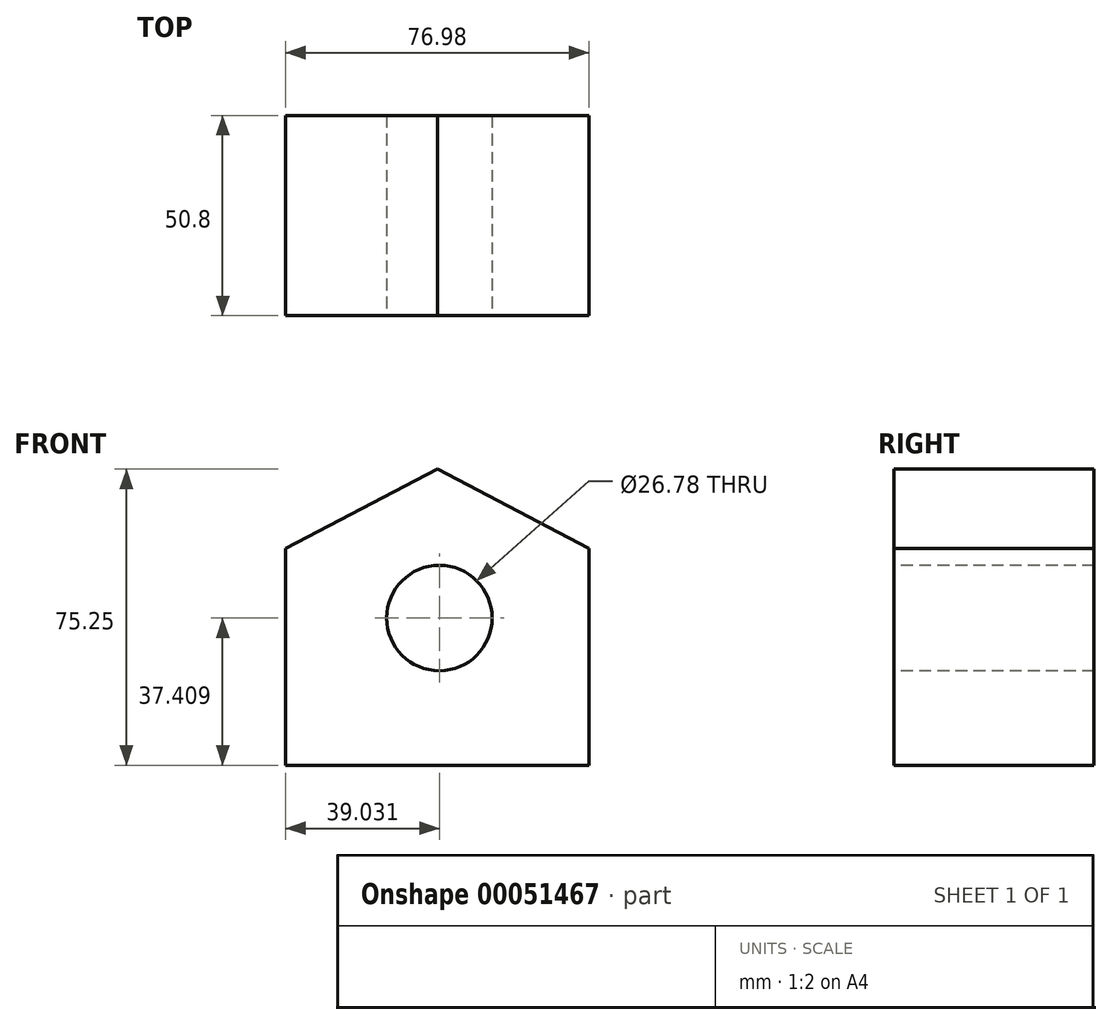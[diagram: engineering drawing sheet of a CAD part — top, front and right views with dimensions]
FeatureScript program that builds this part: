
annotation { "Feature Type Name" : "Feature", "Feature Type Description" : "" }
export const myFeature = defineFeature(function(context is Context, id is Id, definition is map)
    precondition{}
    {
        {
            var Q0;
            Q0=qCreatedBy(makeId("Front.planeOp"),FACE);
            var sketch = newSketch(context, id + "F0", { "sketchPlane" : qUnion([Q0])});
            skLineSegment(sketch, "E0", {"start": v(0, 69.63) * mm, "end": v(0, 9.95) * mm, "construction": true});
            skLineSegment(sketch, "E1", {"start": v(0, 58.6) * mm, "end": v(-38.5, 38.5) * mm});
            skLineSegment(sketch, "E2", {"start": v(-38.5, 38.5) * mm, "end": v(-38.5, -16.65) * mm});
            skLineSegment(sketch, "E3.MirrorCS", {"start": v(0, 58.6) * mm, "end": v(38.5, 38.5) * mm});
            skLineSegment(sketch, "E4.MirrorCS", {"start": v(38.5, 38.5) * mm, "end": v(38.5, -16.65) * mm});
            skLineSegment(sketch, "E5", {"start": v(-38.5, -16.65) * mm, "end": v(38.5, -16.65) * mm});
            skSolve(sketch);
        }
        {
            var Q0;
            Q0 = qSketchRegion(id + "F0", true);
            extrude(context, id + "F1", {"entities" : qUnion([Q0]), "oppositeDirection" : true, "depth" : 50.8 * mm});
        }
        {
            var Q0;
            Q0=qCreatedBy(makeId("Front.planeOp"),FACE);
            var sketch = newSketch(context, id + "F2", { "sketchPlane" : qUnion([Q0])});
            skLineSegment(sketch, "E6", {"start": v(-52.33, 20.76) * mm, "end": v(53.41, 20.76) * mm, "construction": true});
            skCircle(sketch, "E7", {"center": v(0.54, 20.76) * mm, "radius": 13.4 * mm});
            skSolve(sketch);
        }
        {
            var Q0;
            Q0=makeQuery(id+"F2.imprint","IMPRINT",FACE,{"disambiguationData":[TD([[makeQuery(id+"F2.imprint","IMPRINT",EDGE,{"derivedFrom":sQuery(id+"F2.wireOp",EDGE,"E7")}),1.0]])]});
            extrude(context, id + "F3", {"entities" : qUnion([Q0]), "operationType" : NewBodyOperationType.REMOVE, "endBound" : BoundingType.THROUGH_ALL, "oppositeDirection" : true, "depth" : 25.4 * mm});
        }
    });
